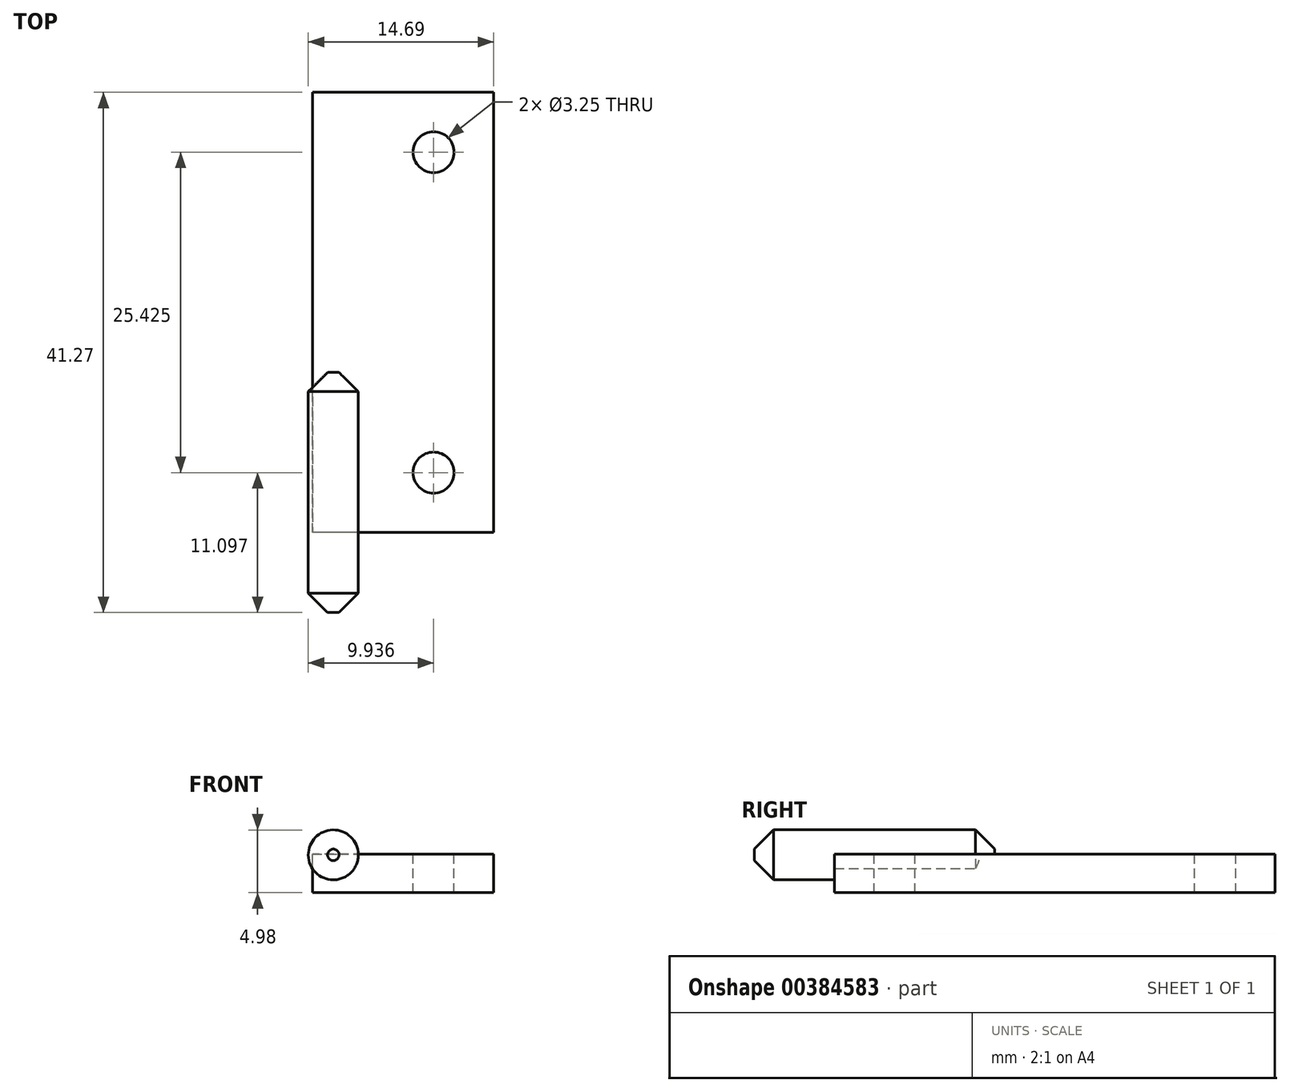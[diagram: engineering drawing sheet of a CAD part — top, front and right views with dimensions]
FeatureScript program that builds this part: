
annotation { "Feature Type Name" : "Feature", "Feature Type Description" : "" }
export const myFeature = defineFeature(function(context is Context, id is Id, definition is map)
    precondition{}
    {
        {
            var Q0;
            Q0=qCreatedBy(makeId("Top.planeOp"),FACE);
            var sketch = newSketch(context, id + "F0", { "sketchPlane" : qUnion([Q0])});
            skLineSegment(sketch, "E0.bottom", {"start": v(7.18, 17.46) * mm, "end": v(-7.18, 17.46) * mm});
            skLineSegment(sketch, "E0.top", {"start": v(7.18, -17.46) * mm, "end": v(-7.18, -17.46) * mm});
            skLineSegment(sketch, "E0.left", {"start": v(7.18, 17.46) * mm, "end": v(7.18, -17.46) * mm});
            skLineSegment(sketch, "E0.right", {"start": v(-7.18, 17.46) * mm, "end": v(-7.18, -17.46) * mm});
            skPoint(sketch, "E0.middle", {"position": v(0, 0) * mm});
            skLineSegment(sketch, "E1", {"start": v(2.43, 17.46) * mm, "end": v(2.43, -17.46) * mm, "construction": true});
            skCircle(sketch, "E2", {"center": v(2.43, 12.71) * mm, "radius": 1.63 * mm});
            skCircle(sketch, "E3.MirrorC", {"center": v(2.43, -12.71) * mm, "radius": 1.63 * mm});
            skLineSegment(sketch, "E4", {"start": v(-5.52, 17.46) * mm, "end": v(-5.52, -17.46) * mm, "construction": true});
            skSolve(sketch);
        }
        {
            var Q0;
            Q0 = qSketchRegion(id + "F0", true);
            extrude(context, id + "F1", {"entities" : qUnion([Q0]), "oppositeDirection" : true, "depth" : 1.02 * mm, "hasSecondDirection" : true, "secondDirectionOppositeDirection" : false, "secondDirectionDepth" : 2.03 * mm});
        }
        {
            var Q0;
            Q0=makeQuery(id+"F1.opExtrude","SWEPT_FACE",FACE,{"disambiguationData":[OSD([sQuery(id+"F0.wireOp",EDGE,"E0.top")])]});
            var sketch = newSketch(context, id + "F2", { "sketchPlane" : qUnion([Q0])});
            skCircle(sketch, "E5", {"center": v(-5.52, 1.98) * mm, "radius": 1.98 * mm});
            skSolve(sketch);
        }
        {
            var Q0;
            Q0 = qSketchRegion(id + "F2", true);
            extrude(context, id + "F3", {"entities" : qUnion([Q0]), "operationType" : NewBodyOperationType.ADD, "depth" : 6.35 * mm, "hasSecondDirection" : true, "secondDirectionOppositeDirection" : true, "secondDirectionDepth" : 12.7 * mm});
        }
        {
            var Q0;
            Q0=makeQuery(id+"F3.opExtrude","CAP_EDGE",EDGE,{"disambiguationData":[OSD([sQuery(id+"F2.wireOp",EDGE,"E5")])],"isStart":false});
            var Q1;
            Q1=makeQuery(id+"F3.opExtrude","CAP_EDGE",EDGE,{"disambiguationData":[OSD([sQuery(id+"F2.wireOp",EDGE,"E5")])],"isStart":true});
            chamfer(context, id + "F4", {"entities" : qUnion([Q0, Q1]), "width" : 1.52 * mm, "tangentPropagation" : true});
        }
    });
